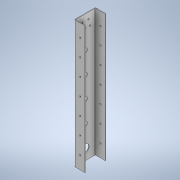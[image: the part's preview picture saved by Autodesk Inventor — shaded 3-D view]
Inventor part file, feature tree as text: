
AUTODESK INVENTOR PART (.ipt)
format: ipt  version: 2022 (Build 260153000, 153)  size: 259,584 bytes
history: native  units: mm
features: sketch x5, projected_geometry x4, sheet_metal_op x3, extrude x3, other x3
ambient origin geometry x8: Origin, YZ Plane, XZ Plane, XY Plane, X Axis, Y Axis, Z Axis, Center Point
bodies: Solid1 (feature_tree)
feature tree (18):
  sheet_metal_op  "Contour Flange1"
  extrude  "Extrusion3"  Depth=25.0mm
  extrude  "Extrusion4"  Depth=1.5mm
  extrude  "Extrusion5"  Depth=1.5mm
  sketch  "Sketch1"  dims[d0=50.0mm d1=25.0mm]
  other  "Plate1"
  sheet_metal_op  "Bend1"
  sheet_metal_op  "Corner1"
  sketch  "Sketch2"  dims[d2=25.0mm d3=1.5mm]
  projected_geometry  "Projected Loop1"
  sketch  "Sketch8"  dims[d4=1.5mm d5=0.75mm]
  projected_geometry  "Projected Loop9"
  sketch  "Sketch9"  dims[d6=3.0mm]
  projected_geometry  "Projected Loop10"
  sketch  "Sketch10"  dims[d7=1.5mm d8=300.0mm d9=1.5mm d10=0.5mm d11=6.0mm d12=1.5mm d13=1.5mm d14=10.0mm d15=25.0mm d16=22.0mm d17=50.0mm d19=50.0mm d20=10.0mm d22=10.0mm d24=1.5mm d25=0.0mm d33=44.0mm d34=3.35mm d35=3.35mm d36=3.35mm d37=3.35mm d38=3.35mm d39=44.0mm d40=14.666667mm d43=14.666667mm d46=14.666667mm d47=11.0mm d48=11.0mm d49=11.0mm d50=10.0mm d51=0.0mm d52=14.666667mm d53=14.666667mm d54=14.666667mm d55=14.666667mm d56=14.666667mm d57=14.666667mm d58=3.35mm d59=30.0mm d60=70.0mm d62=40.0mm d63=10.0mm d65=10.0mm d67=0.0mm d68=0.0mm d69=18.0mm d70=0.0mm d71=0.0mm]
  projected_geometry  "Projected Loop11"
  other  "Cut1"
  other  "Definition1"
